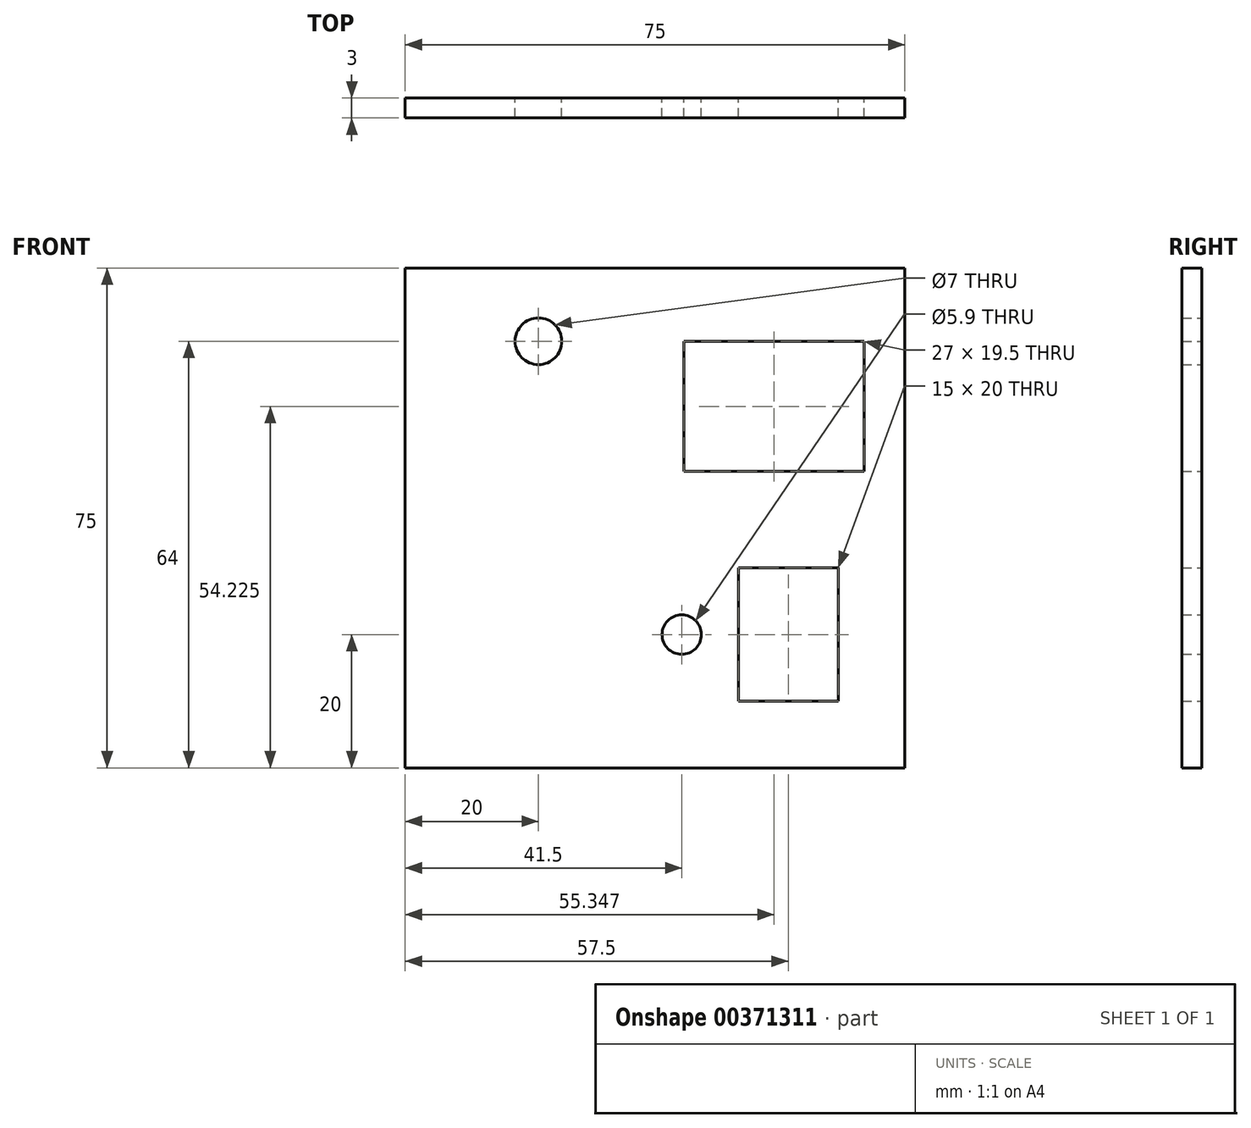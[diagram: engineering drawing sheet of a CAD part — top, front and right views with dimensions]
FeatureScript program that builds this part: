
annotation { "Feature Type Name" : "Feature", "Feature Type Description" : "" }
export const myFeature = defineFeature(function(context is Context, id is Id, definition is map)
    precondition{}
    {
        {
            var Q0;
            Q0=qCreatedBy(makeId("Front.planeOp"),FACE);
            var sketch = newSketch(context, id + "F0", { "sketchPlane" : qUnion([Q0])});
            skLineSegment(sketch, "E0.bottom", {"start": v(37.5, 37.5) * mm, "end": v(-37.5, 37.5) * mm});
            skLineSegment(sketch, "E0.top", {"start": v(37.5, -37.5) * mm, "end": v(-37.5, -37.5) * mm});
            skLineSegment(sketch, "E0.left", {"start": v(37.5, 37.5) * mm, "end": v(37.5, -37.5) * mm});
            skLineSegment(sketch, "E0.right", {"start": v(-37.5, 37.5) * mm, "end": v(-37.5, -37.5) * mm});
            skPoint(sketch, "E0.middle", {"position": v(0, 0) * mm});
            skCircle(sketch, "E1", {"center": v(0, 0) * mm, "radius": 5.5 * mm, "construction": true});
            skCircle(sketch, "E2", {"center": v(-17.5, 26.5) * mm, "radius": 3.5 * mm});
            skLineSegment(sketch, "E3.bottom", {"start": v(4.35, 26.47) * mm, "end": v(31.35, 26.47) * mm});
            skLineSegment(sketch, "E3.top", {"start": v(4.35, 6.97) * mm, "end": v(31.35, 6.97) * mm});
            skLineSegment(sketch, "E3.left", {"start": v(4.35, 26.47) * mm, "end": v(4.35, 6.97) * mm});
            skLineSegment(sketch, "E3.right", {"start": v(31.35, 26.47) * mm, "end": v(31.35, 6.97) * mm});
            skLineSegment(sketch, "E4.bottom", {"start": v(12.5, -7.5) * mm, "end": v(27.5, -7.5) * mm});
            skLineSegment(sketch, "E4.top", {"start": v(12.5, -27.5) * mm, "end": v(27.5, -27.5) * mm});
            skLineSegment(sketch, "E4.left", {"start": v(12.5, -7.5) * mm, "end": v(12.5, -27.5) * mm});
            skLineSegment(sketch, "E4.right", {"start": v(27.5, -7.5) * mm, "end": v(27.5, -27.5) * mm});
            skLineSegment(sketch, "E5.bottom", {"start": v(-35.36, 14.84) * mm, "end": v(-4.36, 14.84) * mm, "construction": true});
            skLineSegment(sketch, "E5.top", {"start": v(-35.36, -32.16) * mm, "end": v(-4.36, -32.16) * mm, "construction": true});
            skLineSegment(sketch, "E5.left", {"start": v(-35.36, 14.84) * mm, "end": v(-35.36, -32.16) * mm, "construction": true});
            skLineSegment(sketch, "E5.right", {"start": v(-4.36, 14.84) * mm, "end": v(-4.36, -32.16) * mm, "construction": true});
            skCircle(sketch, "E6", {"center": v(-17.5, 26.5) * mm, "radius": 8.5 * mm, "construction": true});
            skLineSegment(sketch, "E7", {"start": v(0, 0) * mm, "end": v(33.23, 33.23) * mm, "construction": true});
            skCircle(sketch, "E8", {"center": v(33.23, 33.23) * mm, "radius": 3.5 * mm, "construction": true});
            skLineSegment(sketch, "E9.bottom", {"start": v(4.35, 30.97) * mm, "end": v(31.35, 30.97) * mm, "construction": true});
            skLineSegment(sketch, "E9.top", {"start": v(4.35, 2.97) * mm, "end": v(31.35, 2.97) * mm, "construction": true});
            skLineSegment(sketch, "E9.left", {"start": v(4.35, 30.97) * mm, "end": v(4.35, 2.97) * mm, "construction": true});
            skLineSegment(sketch, "E9.right", {"start": v(31.35, 30.97) * mm, "end": v(31.35, 2.97) * mm, "construction": true});
            skCircle(sketch, "E10", {"center": v(4, -17.5) * mm, "radius": 2.95 * mm});
            skLineSegment(sketch, "E11.bottom", {"start": v(10.5, -11) * mm, "end": v(-2.5, -11) * mm, "construction": true});
            skLineSegment(sketch, "E11.top", {"start": v(10.5, -24) * mm, "end": v(-2.5, -24) * mm, "construction": true});
            skLineSegment(sketch, "E11.left", {"start": v(10.5, -11) * mm, "end": v(10.5, -24) * mm, "construction": true});
            skLineSegment(sketch, "E11.right", {"start": v(-2.5, -11) * mm, "end": v(-2.5, -24) * mm, "construction": true});
            skCircle(sketch, "E12.1.0", {"center": v(-33.23, 33.23) * mm, "radius": 3.5 * mm, "construction": true});
            skCircle(sketch, "E12.2.0", {"center": v(-33.23, -33.23) * mm, "radius": 3.5 * mm, "construction": true});
            skCircle(sketch, "E12.3.0", {"center": v(33.23, -33.23) * mm, "radius": 3.5 * mm, "construction": true});
            skSolve(sketch);
        }
        {
            var Q0;
            Q0 = qSketchRegion(id + "F0", true);
            extrude(context, id + "F1", {"entities" : qUnion([Q0]), "depth" : 3 * mm});
        }
    });
